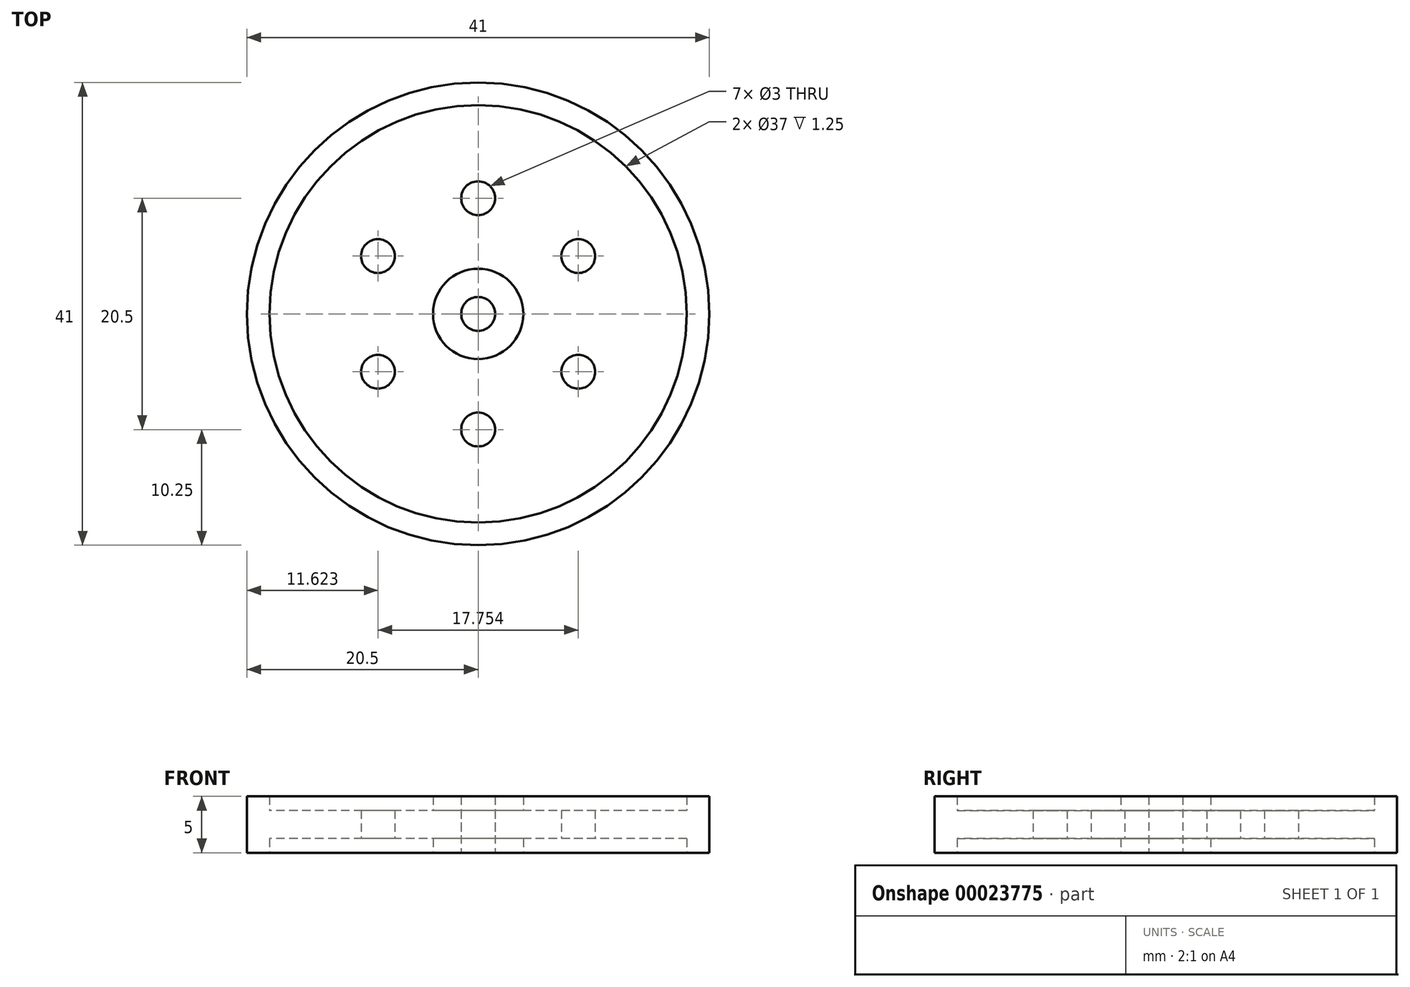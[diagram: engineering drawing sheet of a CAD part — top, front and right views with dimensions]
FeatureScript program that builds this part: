
annotation { "Feature Type Name" : "Feature", "Feature Type Description" : "" }
export const myFeature = defineFeature(function(context is Context, id is Id, definition is map)
    precondition{}
    {
        {
            var Q0;
            Q0=qCreatedBy(makeId("Top.planeOp"),FACE);
            var sketch = newSketch(context, id + "F0", { "sketchPlane" : qUnion([Q0])});
            skCircle(sketch, "E0", {"center": v(0, 0) * mm, "radius": 20.5 * mm});
            skCircle(sketch, "E1", {"center": v(0, 0) * mm, "radius": 1.5 * mm});
            skCircle(sketch, "E2", {"center": v(0, 0) * mm, "radius": 4 * mm});
            skCircle(sketch, "E3", {"center": v(0, 0) * mm, "radius": 18.5 * mm});
            skLineSegment(sketch, "E4", {"start": v(0, 0) * mm, "end": v(0, 20.5) * mm, "construction": true});
            skPoint(sketch, "E5", {"position": v(0, 10.25) * mm});
            skCircle(sketch, "E6", {"center": v(0, 0) * mm, "radius": 10.25 * mm, "construction": true});
            skLineSegment(sketch, "E7", {"start": v(0, 0) * mm, "end": v(8.88, 5.13) * mm, "construction": true});
            skLineSegment(sketch, "E8", {"start": v(0, 0) * mm, "end": v(17.75, -10.25) * mm, "construction": true});
            skLineSegment(sketch, "E9", {"start": v(0, 0) * mm, "end": v(0, -20.5) * mm, "construction": true});
            skLineSegment(sketch, "E10", {"start": v(0, 0) * mm, "end": v(-17.75, 10.25) * mm, "construction": true});
            skLineSegment(sketch, "E11", {"start": v(0, 0) * mm, "end": v(-17.75, -10.25) * mm, "construction": true});
            skCircle(sketch, "E12", {"center": v(-8.88, 5.12) * mm, "radius": 1.5 * mm});
            skCircle(sketch, "E13", {"center": v(0, 10.25) * mm, "radius": 1.5 * mm});
            skCircle(sketch, "E14", {"center": v(8.88, 5.13) * mm, "radius": 1.5 * mm});
            skCircle(sketch, "E15", {"center": v(8.88, -5.12) * mm, "radius": 1.5 * mm});
            skCircle(sketch, "E16", {"center": v(0, -10.25) * mm, "radius": 1.5 * mm});
            skCircle(sketch, "E17", {"center": v(-8.88, -5.13) * mm, "radius": 1.5 * mm});
            skSolve(sketch);
        }
        {
            var Q0;
            Q0 = qSketchRegion(id + "F0", true);
            extrude(context, id + "F1", {"entities" : qUnion([Q0]), "depth" : 5 * mm});
        }
        {
            var Q0;
            Q0=makeQuery(id+"F0.imprint","IMPRINT",FACE,{"disambiguationData":[TD([[makeQuery(id+"F0.imprint","IMPRINT",EDGE,{"derivedFrom":sQuery(id+"F0.wireOp",EDGE,"E2")}),-1.0]])]});
            extrude(context, id + "F2", {"entities" : qUnion([Q0]), "operationType" : NewBodyOperationType.ADD, "depth" : 2.5 * mm + 1.25 * mm});
        }
        {
            var Q0;
            Q0=makeQuery(id+"F0.imprint","IMPRINT",FACE,{"disambiguationData":[TD([[makeQuery(id+"F0.imprint","IMPRINT",EDGE,{"derivedFrom":sQuery(id+"F0.wireOp",EDGE,"E2")}),-1.0]])]});
            extrude(context, id + "F3", {"entities" : qUnion([Q0]), "operationType" : NewBodyOperationType.REMOVE, "depth" : 1.25 * mm});
        }
        {
            var Q0;
            Q0=makeQuery(id+"F0.imprint","IMPRINT",FACE,{"disambiguationData":[TD([[makeQuery(id+"F0.imprint","IMPRINT",EDGE,{"derivedFrom":sQuery(id+"F0.wireOp",EDGE,"E1")}),-1.0]])]});
            extrude(context, id + "F4", {"entities" : qUnion([Q0]), "operationType" : NewBodyOperationType.ADD, "depth" : 5 * mm});
        }
    });
